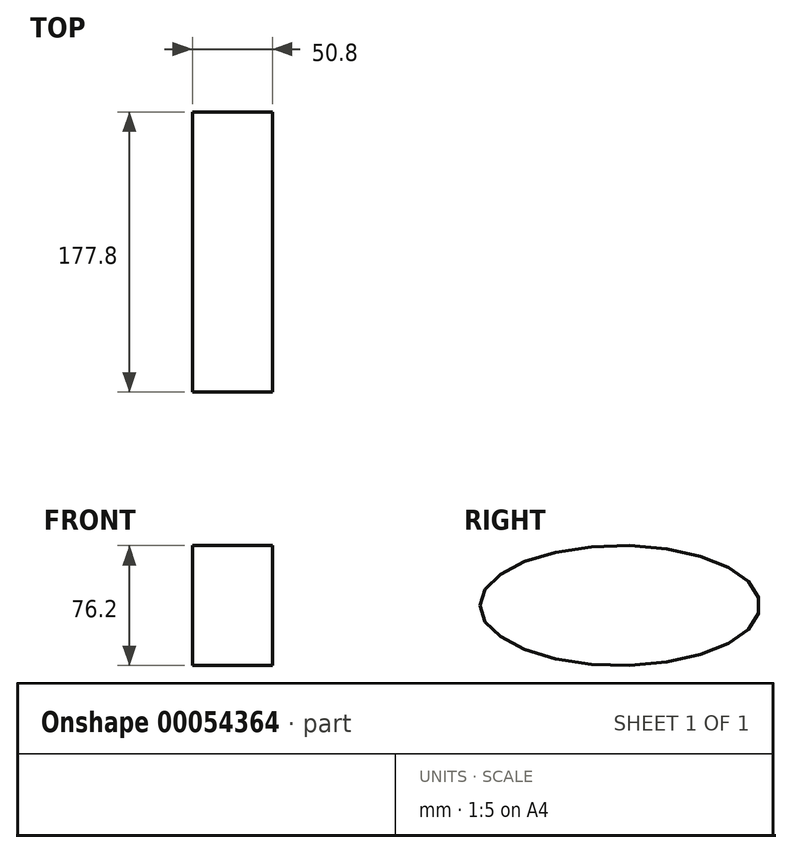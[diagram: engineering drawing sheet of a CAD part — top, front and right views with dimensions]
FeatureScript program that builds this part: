
annotation { "Feature Type Name" : "Feature", "Feature Type Description" : "" }
export const myFeature = defineFeature(function(context is Context, id is Id, definition is map)
    precondition{}
    {
        {
            var Q0;
            Q0=qCreatedBy(makeId("Right.planeOp"),FACE);
            var sketch = newSketch(context, id + "F0", { "sketchPlane" : qUnion([Q0])});
            skEllipse(sketch, "E0", {"center": v(0, 0) * mm, "majorRadius": 38.1 * mm, "minorRadius": 88.9 * mm, "majorAxis": v(0, 1)});
            skSolve(sketch);
        }
        {
            var Q0;
            Q0 = qSketchRegion(id + "F0", true);
            extrude(context, id + "F1", {"entities" : qUnion([Q0]), "depth" : 50.8 * mm});
        }
    });
